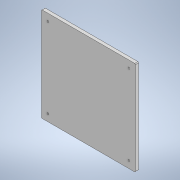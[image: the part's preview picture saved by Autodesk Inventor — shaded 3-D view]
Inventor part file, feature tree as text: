
AUTODESK INVENTOR PART (.ipt)
format: ipt  version: 2020.2 (Build 242310000, 310)  size: 118,272 bytes
history: native  units: mm
features: sketch x2, extrude x1, hole x1, fillet x1
ambient origin geometry x8: Origin, YZ Plane, XZ Plane, XY Plane, X Axis, Y Axis, Z Axis, Center Point
bodies: Solide1 (feature_tree)
feature tree (5):
  extrude  "Extrusion1"  Depth=180.0mm
  hole  "Perçage1"  [1 undecoded]
  fillet  "Congé2"  Radius=6.0mm
  sketch  "Esquisse1"
  sketch  "Esquisse2"
note: 1 required parameter value undecoded (feature->parameter linkage not recoverable at this tier; creation-order binding heuristic only, values carry confidence <= 0.55)
